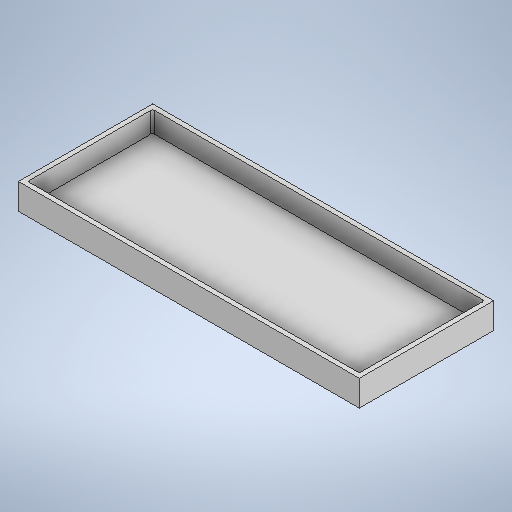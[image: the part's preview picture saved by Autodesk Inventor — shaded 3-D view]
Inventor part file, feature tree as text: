
AUTODESK INVENTOR PART (.ipt)
format: ipt  version: 2025 (Build 290162000, 162)  size: 240,128 bytes
history: native  units: mm
features: extrude x2, sketch x2, fillet x1
ambient origin geometry x8: Origin, YZ Plane, XZ Plane, XY Plane, X Axis, Y Axis, Z Axis, Center Point
bodies: Solid1 (feature_tree)
feature tree (5):
  extrude  "Extrusion1"  Depth=130.0mm
  extrude  "Extrusion2"  Depth=321.0mm
  fillet  "Fillet1"  Radius=121.0mm
  sketch  "Sketch1"  dims[d0=330.0mm d1=130.0mm]
  sketch  "Sketch2"  dims[d2=25.0mm d3=0.0mm d4=321.0mm d5=121.0mm d6=20.0mm d7=0.0mm d8=2.0mm]
